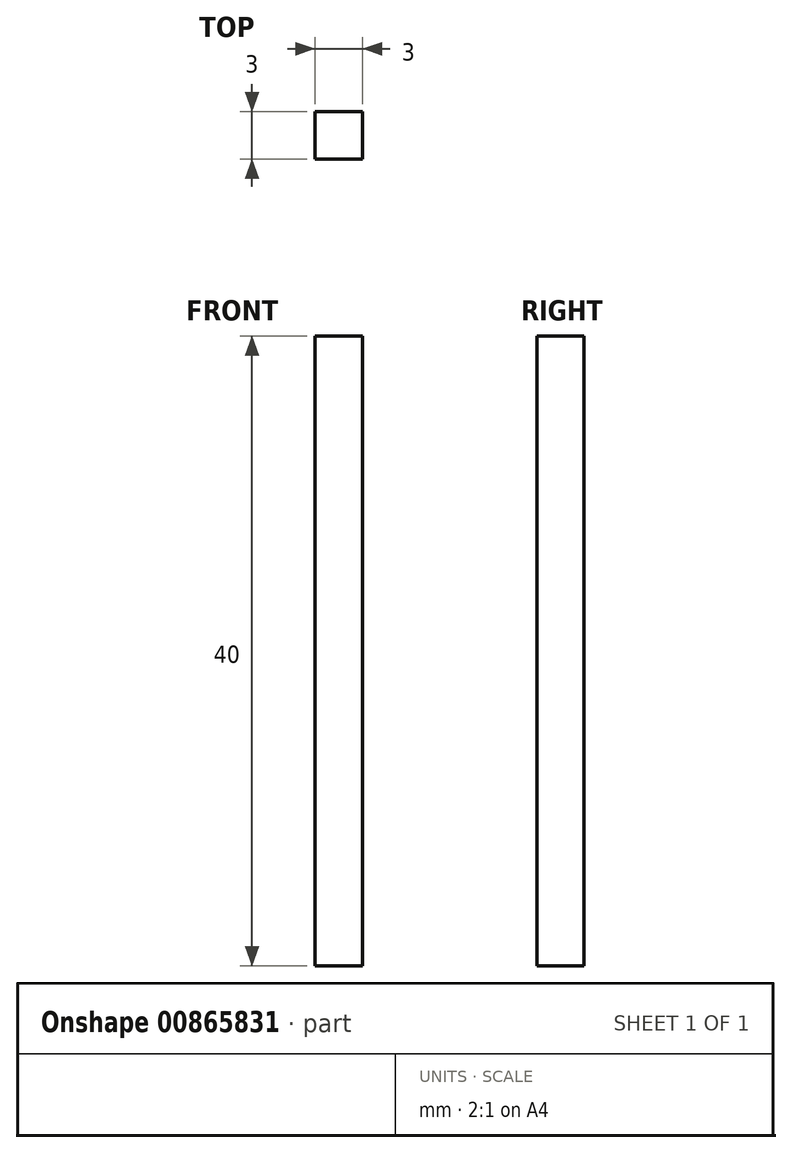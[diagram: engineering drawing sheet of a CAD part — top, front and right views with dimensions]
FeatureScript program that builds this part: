
annotation { "Feature Type Name" : "Feature", "Feature Type Description" : "" }
export const myFeature = defineFeature(function(context is Context, id is Id, definition is map)
    precondition{}
    {
        {
            var Q0;
            Q0=qCreatedBy(makeId("Top.planeOp"),FACE);
            var sketch = newSketch(context, id + "F0", { "sketchPlane" : qUnion([Q0])});
            skLineSegment(sketch, "E0.bottom", {"start": v(-1.5, 1.5) * mm, "end": v(1.5, 1.5) * mm});
            skLineSegment(sketch, "E0.top", {"start": v(-1.5, -1.5) * mm, "end": v(1.5, -1.5) * mm});
            skLineSegment(sketch, "E0.left", {"start": v(-1.5, 1.5) * mm, "end": v(-1.5, -1.5) * mm});
            skLineSegment(sketch, "E0.right", {"start": v(1.5, 1.5) * mm, "end": v(1.5, -1.5) * mm});
            skSolve(sketch);
        }
        {
            var Q0;
            Q0=makeQuery(id+"F0.imprint","IMPRINT",FACE,{"disambiguationData":[TD([[makeQuery(id+"F0.imprint","IMPRINT",EDGE,{"derivedFrom":sQuery(id+"F0.wireOp",EDGE,"E0.bottom")}),-1.0]])]});
            extrude(context, id + "F1", {"entities" : qUnion([Q0]), "depth" : 40 * mm, "offsetDistance" : 25 * mm});
        }
    });
